# Revit family: 3D-AKE-00049942
name_source: partatom
category: Allgemeines Modell
units: mm (PartAtom-declared; Revit-internal decimal feet)

## family parameters
Arbeitsebenenbasiert = Nein
Beim Laden mit Abzugskörper schneiden = Nein
Bemaßung runder Anschluss = Durchmesser verwenden
Beschriftungsausrichtung beibehalten = Nein
Gemeinsam genutzt = Nein
Immer vertikal = Ja
Kann Basisbauteil für Bewehrung sein = Nein
Raumberechnungspunkt = Nein
Teiletyp = Normal

## types (1)
- Norm
    Abwicklungshöhe = 0
    Abwicklungslänge = 0
    Artikelvorlage = 00900016
    Bauteilnummer = 3D-AKE-00049942
    Breite = 2070
    DocNumber = 3D-AKE-00049942
    Entstanden aus = 3D-AKE-00049940.ipt
    Ersatzteilkennung = nein
    Erstellungsdatum = 16.05.2024
    Folder = Kunden\Vereinfachte Modelle\vereinfachte Modelle- Abänderung für Hainzl Steuerung\
    Genehmigungsdatum Konstr. = 12.06.2024
    Gewicht = 2915,35 kg
    Höhe = 655
    Kennung = Standardteil
    Konstruktionsstatus = 1
    Revisionsnummer = -
    Tiefe = 705
    Titel = UKW 6-1-E R290
    VDS_Category = 3D-Konstruktion Bauteil
    Vorgabe-Ansicht = 0 mm  [stored 0 ft]

note: [stored X ft] marks values corroborated as IEEE doubles in the binary element streams (Revit-internal decimal feet)
